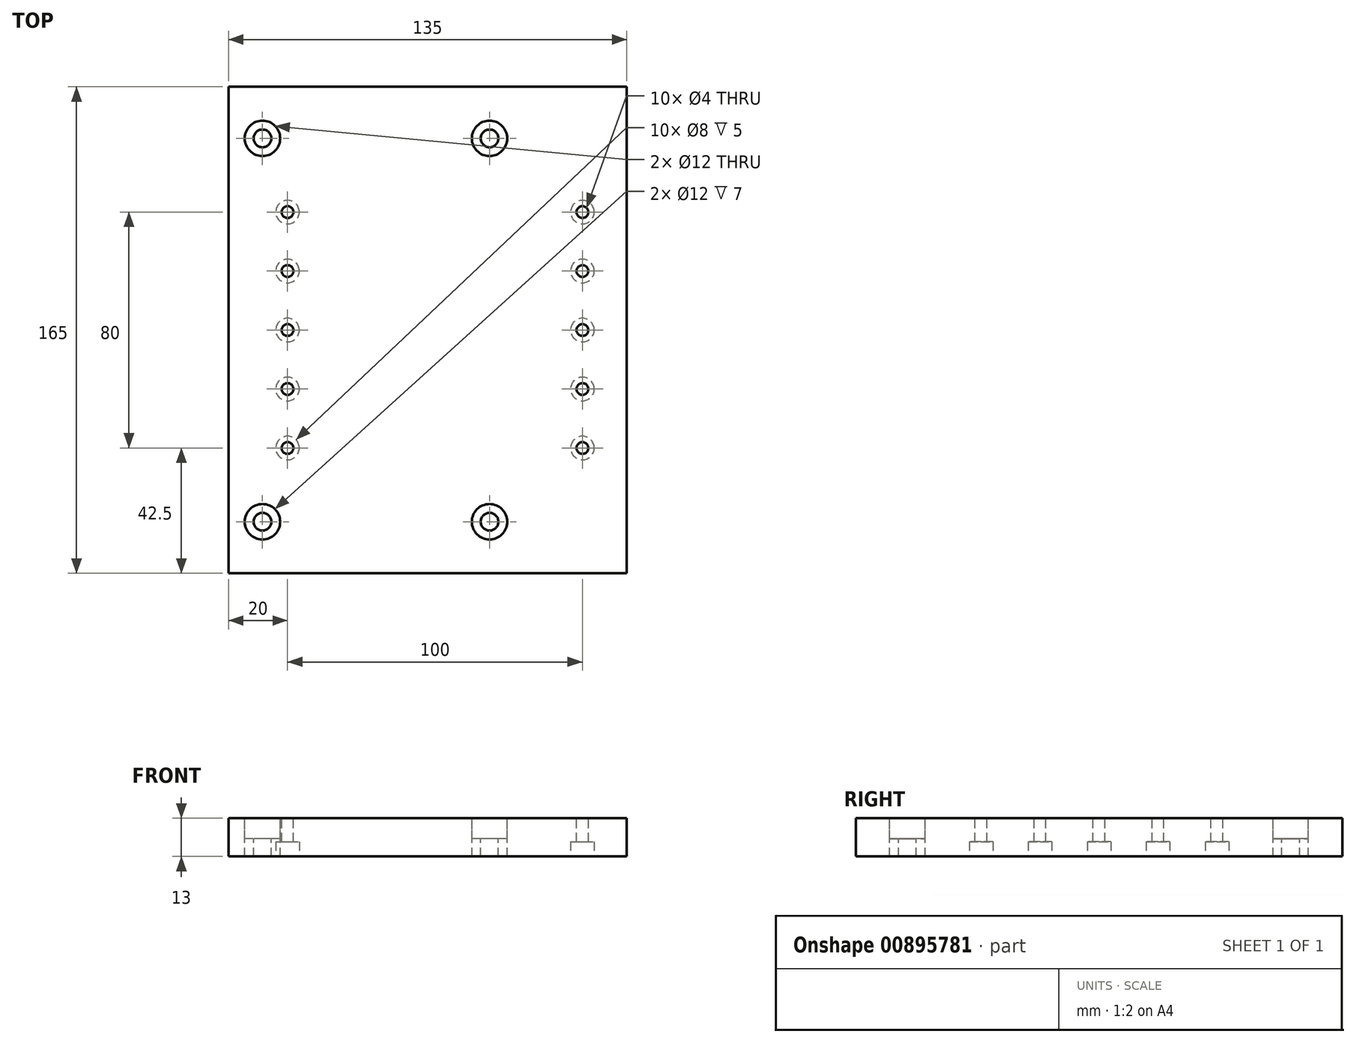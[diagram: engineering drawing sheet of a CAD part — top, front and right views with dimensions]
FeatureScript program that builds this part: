
annotation { "Feature Type Name" : "Feature", "Feature Type Description" : "" }
export const myFeature = defineFeature(function(context is Context, id is Id, definition is map)
    precondition{}
    {
        {
            var Q0;
            Q0=qCreatedBy(makeId("Top.planeOp"),FACE);
            var sketch = newSketch(context, id + "F0", { "sketchPlane" : qUnion([Q0])});
            skLineSegment(sketch, "E0.bottom", {"start": v(-50, 82.5) * mm, "end": v(85, 82.5) * mm});
            skLineSegment(sketch, "E0.top", {"start": v(-50, -82.5) * mm, "end": v(85, -82.5) * mm});
            skLineSegment(sketch, "E0.left", {"start": v(-50, 82.5) * mm, "end": v(-50, -82.5) * mm});
            skLineSegment(sketch, "E0.right", {"start": v(85, 82.5) * mm, "end": v(85, -82.5) * mm});
            skCircle(sketch, "E1", {"center": v(38.5, 65) * mm, "radius": 3 * mm});
            skCircle(sketch, "E2.MirrorC", {"center": v(38.5, -65) * mm, "radius": 3 * mm});
            skCircle(sketch, "E3.MirrorC", {"center": v(-38.5, -65) * mm, "radius": 3 * mm});
            skCircle(sketch, "E4.MirrorC", {"center": v(-38.5, 65) * mm, "radius": 3 * mm});
            skCircle(sketch, "E5", {"center": v(70, 0) * mm, "radius": 2 * mm});
            skCircle(sketch, "E6.MirrorC", {"center": v(70, -40) * mm, "radius": 2 * mm});
            skCircle(sketch, "E7.MirrorC", {"center": v(-30, -40) * mm, "radius": 2 * mm});
            skCircle(sketch, "E8", {"center": v(-30, -20) * mm, "radius": 2 * mm});
            skCircle(sketch, "E9", {"center": v(70, -20) * mm, "radius": 2 * mm});
            skCircle(sketch, "E10.MirrorC", {"center": v(-30, 20) * mm, "radius": 2 * mm});
            skCircle(sketch, "E11.MirrorC", {"center": v(70, 20) * mm, "radius": 2 * mm});
            skCircle(sketch, "E12.MirrorC", {"center": v(-30, 40) * mm, "radius": 2 * mm});
            skCircle(sketch, "E13.MirrorC", {"center": v(70, 40) * mm, "radius": 2 * mm});
            skLineSegment(sketch, "E14.MirrorCS", {"start": v(85, -82.5) * mm, "end": v(85, 82.5) * mm});
            skCircle(sketch, "E15", {"center": v(-30, 0) * mm, "radius": 2 * mm});
            skCircle(sketch, "E16", {"center": v(38.5, 65) * mm, "radius": 6 * mm});
            skCircle(sketch, "E17", {"center": v(38.5, -65) * mm, "radius": 6 * mm});
            skCircle(sketch, "E18", {"center": v(-38.5, -65) * mm, "radius": 6 * mm});
            skCircle(sketch, "E19", {"center": v(-38.5, 65) * mm, "radius": 6 * mm});
            skSolve(sketch);
        }
        {
            var Q0;
            Q0=makeQuery(id+"F0.imprint","IMPRINT",FACE,{"disambiguationData":[TD([[makeQuery(id+"F0.imprint","IMPRINT",EDGE,{"derivedFrom":sQuery(id+"F0.wireOp",EDGE,"E0.bottom")}),-1.0]])]});
            var Q1;
            Q1=makeQuery(id+"F0.imprint","IMPRINT",FACE,{"disambiguationData":[TD([[makeQuery(id+"F0.imprint","IMPRINT",EDGE,{"derivedFrom":sQuery(id+"F0.wireOp",EDGE,"E4.MirrorC")}),1.0]])]});
            var Q2;
            Q2=makeQuery(id+"F0.imprint","IMPRINT",FACE,{"disambiguationData":[TD([[makeQuery(id+"F0.imprint","IMPRINT",EDGE,{"derivedFrom":sQuery(id+"F0.wireOp",EDGE,"E1")}),-1.0]])]});
            var Q3;
            Q3=makeQuery(id+"F0.imprint","IMPRINT",FACE,{"disambiguationData":[TD([[makeQuery(id+"F0.imprint","IMPRINT",EDGE,{"derivedFrom":sQuery(id+"F0.wireOp",EDGE,"E2.MirrorC")}),1.0]])]});
            var Q4;
            Q4=makeQuery(id+"F0.imprint","IMPRINT",FACE,{"disambiguationData":[TD([[makeQuery(id+"F0.imprint","IMPRINT",EDGE,{"derivedFrom":sQuery(id+"F0.wireOp",EDGE,"E3.MirrorC")}),-1.0]])]});
            extrude(context, id + "F1", {"entities" : qUnion([Q0, Q1, Q2, Q3, Q4]), "oppositeDirection" : true, "offsetDistance" : 25 * mm, "depth" : 13 * mm});
        }
        {
            var Q0;
            Q0=makeQuery(id+"F0.imprint","IMPRINT",FACE,{"disambiguationData":[TD([[makeQuery(id+"F0.imprint","IMPRINT",EDGE,{"derivedFrom":sQuery(id+"F0.wireOp",EDGE,"E0.bottom")}),-1.0]])]});
            var sketch = newSketch(context, id + "F2", { "sketchPlane" : qUnion([Q0])});
            skSolve(sketch);
        }
        {
            var Q0;
            Q0=makeQuery(id+"F0.imprint","IMPRINT",FACE,{"disambiguationData":[TD([[makeQuery(id+"F0.imprint","IMPRINT",EDGE,{"derivedFrom":sQuery(id+"F0.wireOp",EDGE,"E4.MirrorC")}),1.0]])]});
            var Q1;
            Q1=makeQuery(id+"F0.imprint","IMPRINT",FACE,{"disambiguationData":[TD([[makeQuery(id+"F0.imprint","IMPRINT",EDGE,{"derivedFrom":sQuery(id+"F0.wireOp",EDGE,"E4.MirrorC")}),-1.0]])]});
            var Q2;
            Q2=makeQuery(id+"F0.imprint","IMPRINT",FACE,{"disambiguationData":[TD([[makeQuery(id+"F0.imprint","IMPRINT",EDGE,{"derivedFrom":sQuery(id+"F0.wireOp",EDGE,"E1")}),-1.0]])]});
            var Q3;
            Q3=makeQuery(id+"F0.imprint","IMPRINT",FACE,{"disambiguationData":[TD([[makeQuery(id+"F0.imprint","IMPRINT",EDGE,{"derivedFrom":sQuery(id+"F0.wireOp",EDGE,"E1")}),1.0]])]});
            var Q4;
            Q4=makeQuery(id+"F0.imprint","IMPRINT",FACE,{"disambiguationData":[TD([[makeQuery(id+"F0.imprint","IMPRINT",EDGE,{"derivedFrom":sQuery(id+"F0.wireOp",EDGE,"E3.MirrorC")}),-1.0]])]});
            var Q5;
            Q5=makeQuery(id+"F0.imprint","IMPRINT",FACE,{"disambiguationData":[TD([[makeQuery(id+"F0.imprint","IMPRINT",EDGE,{"derivedFrom":sQuery(id+"F0.wireOp",EDGE,"E2.MirrorC")}),1.0]])]});
            var Q6;
            Q6=makeQuery(id+"F0.imprint","IMPRINT",FACE,{"disambiguationData":[TD([[makeQuery(id+"F0.imprint","IMPRINT",EDGE,{"derivedFrom":sQuery(id+"F0.wireOp",EDGE,"E2.MirrorC")}),-1.0]])]});
            var Q7;
            Q7=makeQuery(id+"F2.imprint","IMPRINT",FACE,{"disambiguationData":[TD([[makeQuery(id+"F2.imprint","IMPRINT",EDGE,{"derivedFrom":makeQuery(id+"F0.imprint","IMPRINT",EDGE,{"derivedFrom":sQuery(id+"F0.wireOp",EDGE,"E19")})}),1.0]])]});
            var Q8;
            Q8=makeQuery(id+"F2.imprint","IMPRINT",FACE,{"disambiguationData":[TD([[makeQuery(id+"F2.imprint","IMPRINT",EDGE,{"derivedFrom":makeQuery(id+"F0.imprint","IMPRINT",EDGE,{"derivedFrom":sQuery(id+"F0.wireOp",EDGE,"E18")})}),1.0]])]});
            extrude(context, id + "F3", {"entities" : qUnion([Q0, Q1, Q2, Q3, Q4, Q5, Q6, Q7, Q8]), "operationType" : NewBodyOperationType.REMOVE, "oppositeDirection" : true, "depth" : 7 * mm, "offsetDistance" : 25 * mm});
        }
        {
            var Q0;
            Q0=makeQuery(id+"F1.opExtrude","CAP_FACE",FACE,{"disambiguationData":[OSD([sQuery(id+"F0.wireOp",EDGE,"E0.bottom"),sQuery(id+"F0.wireOp",EDGE,"E0.top"),sQuery(id+"F0.wireOp",EDGE,"E0.left"),sQuery(id+"F0.wireOp",EDGE,"E1"),sQuery(id+"F0.wireOp",EDGE,"E2.MirrorC"),sQuery(id+"F0.wireOp",EDGE,"E3.MirrorC"),sQuery(id+"F0.wireOp",EDGE,"E4.MirrorC"),sQuery(id+"F0.wireOp",EDGE,"E5"),sQuery(id+"F0.wireOp",EDGE,"E6.MirrorC"),sQuery(id+"F0.wireOp",EDGE,"E7.MirrorC"),sQuery(id+"F0.wireOp",EDGE,"E8"),sQuery(id+"F0.wireOp",EDGE,"E9"),sQuery(id+"F0.wireOp",EDGE,"E10.MirrorC"),sQuery(id+"F0.wireOp",EDGE,"E11.MirrorC"),sQuery(id+"F0.wireOp",EDGE,"E12.MirrorC"),sQuery(id+"F0.wireOp",EDGE,"E13.MirrorC"),sQuery(id+"F0.wireOp",EDGE,"E14.MirrorCS"),sQuery(id+"F0.wireOp",EDGE,"E15")])],"isStart":false});
            var sketch = newSketch(context, id + "F4", { "sketchPlane" : qUnion([Q0])});
            skCircle(sketch, "E20", {"center": v(-30, 40) * mm, "radius": 4 * mm});
            skCircle(sketch, "E21", {"center": v(-30, 20) * mm, "radius": 4 * mm});
            skCircle(sketch, "E22", {"center": v(-30, 0) * mm, "radius": 4 * mm});
            skCircle(sketch, "E23", {"center": v(-30, -20) * mm, "radius": 4 * mm});
            skCircle(sketch, "E24", {"center": v(-30, -40) * mm, "radius": 4 * mm});
            skCircle(sketch, "E25", {"center": v(70, 40) * mm, "radius": 4 * mm});
            skCircle(sketch, "E26", {"center": v(70, 0) * mm, "radius": 4 * mm});
            skCircle(sketch, "E27", {"center": v(70, -20) * mm, "radius": 4 * mm});
            skCircle(sketch, "E28", {"center": v(70, -40) * mm, "radius": 4 * mm});
            skPoint(sketch, "E29.center.orphan", {"position": v(70, 20) * mm});
            skCircle(sketch, "E30", {"center": v(70, 20) * mm, "radius": 4 * mm});
            skSolve(sketch);
        }
        {
            var Q0;
            Q0 = qSketchRegion(id + "F4", true);
            extrude(context, id + "F5", {"entities" : qUnion([Q0]), "operationType" : NewBodyOperationType.REMOVE, "oppositeDirection" : true, "depth" : 5 * mm, "offsetDistance" : 25 * mm});
        }
    });
